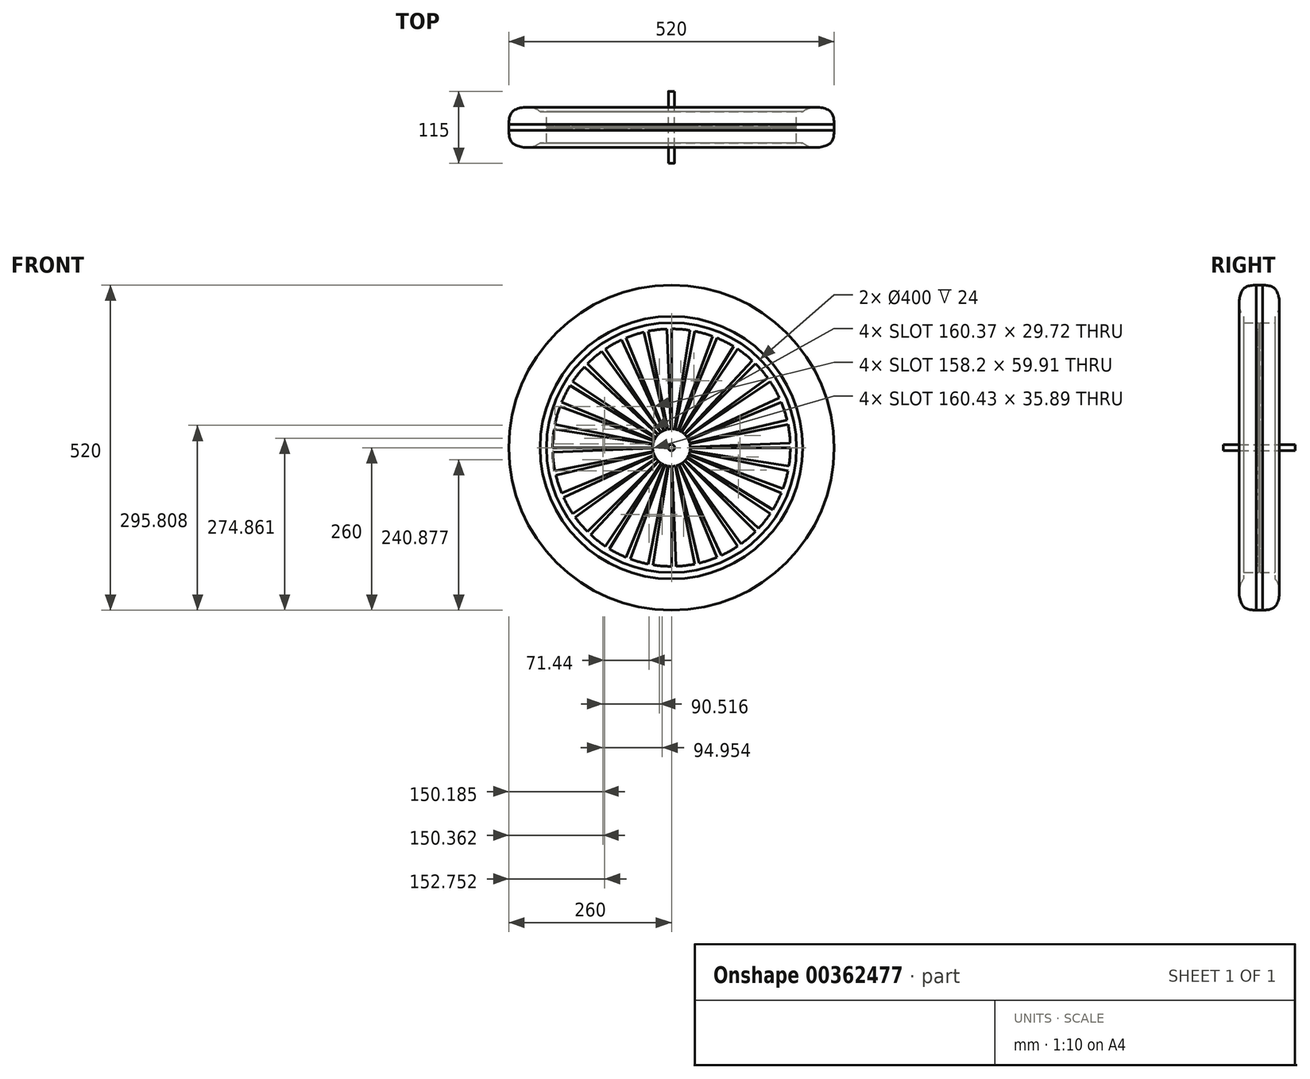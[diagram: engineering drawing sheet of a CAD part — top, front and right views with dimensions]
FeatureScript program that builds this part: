
annotation { "Feature Type Name" : "Feature", "Feature Type Description" : "" }
export const myFeature = defineFeature(function(context is Context, id is Id, definition is map)
    precondition{}
    {
        {
            var Q0;
            Q0=qCreatedBy(makeId("Right.planeOp"),FACE);
            var sketch = newSketch(context, id + "F0", { "sketchPlane" : qUnion([Q0])});
            skLineSegment(sketch, "E0", {"start": v(0, 0) * mm, "end": v(0, 200) * mm, "construction": true});
            skPoint(sketch, "E1.middle", {"position": v(0, 200) * mm});
            skPoint(sketch, "E2.visualSharp", {"position": v(-30.2, 260) * mm});
            skLineSegment(sketch, "E3.left", {"start": v(-1, 200) * mm, "end": v(-1, 5) * mm});
            skLineSegment(sketch, "E4.trimOffspring", {"start": v(-1, 200) * mm, "end": v(-25, 200) * mm});
            skLineSegment(sketch, "E5", {"start": v(-25, 200) * mm, "end": v(-25, 210) * mm});
            skFitSpline(sketch, "E6", {"points": [v(-5, 260) * mm, v(-25.83, 253.38) * mm, v(-32.03, 227.8) * mm, v(-25, 210) * mm], "startDerivative": vector(-86.17, -1.88) * mm, "endDerivative": vector(37.49, -43.12) * mm});
            skLineSegment(sketch, "E7", {"start": v(0, 260) * mm, "end": v(-5, 260) * mm});
            skLineSegment(sketch, "E8", {"start": v(0, 0) * mm, "end": v(-57.5, 0) * mm});
            skLineSegment(sketch, "E9", {"start": v(-57.5, 0) * mm, "end": v(-57.5, 5) * mm});
            skLineSegment(sketch, "E10.MirrorCS", {"start": v(0, 260) * mm, "end": v(5, 260) * mm});
            skLineSegment(sketch, "E11.MirrorCS", {"start": v(25, 200) * mm, "end": v(25, 210) * mm});
            skLineSegment(sketch, "E12.MirrorCS", {"start": v(1, 200) * mm, "end": v(25, 200) * mm});
            skFitSpline(sketch, "E13.MirrorCS", {"points": [v(5, 260) * mm, v(25.83, 253.38) * mm, v(32.03, 227.8) * mm, v(25, 210) * mm], "startDerivative": vector(86.17, -1.88) * mm, "endDerivative": vector(-37.49, -43.12) * mm});
            skLineSegment(sketch, "E14.MirrorCS", {"start": v(57.5, 0) * mm, "end": v(57.5, 5) * mm});
            skLineSegment(sketch, "E15.MirrorCS", {"start": v(0, 0) * mm, "end": v(57.5, 0) * mm});
            skPoint(sketch, "E16.MirrorP", {"position": v(30.2, 260) * mm});
            skLineSegment(sketch, "E17", {"start": v(-57.5, 5) * mm, "end": v(-1, 5) * mm});
            skLineSegment(sketch, "E18.MirrorCS", {"start": v(57.5, 5) * mm, "end": v(1, 5) * mm});
            skLineSegment(sketch, "E19.MirrorCS", {"start": v(1, 200) * mm, "end": v(1, 5) * mm});
            skSolve(sketch);
        }
        {
            var Q0;
            Q0=makeQuery(id+"F0.imprint","IMPRINT",FACE,{"disambiguationData":[TD([[makeQuery(id+"F0.imprint","IMPRINT",EDGE,{"derivedFrom":sQuery(id+"F0.wireOp",EDGE,"E3.left")}),1.0]])]});
            var Q1;
            Q1=sQuery(id+"F0.wireOp",EDGE,"E8");
            revolve(context, id + "F1", {"entities" : qUnion([Q0]), "axis" : qUnion([Q1]), "revolveType" : RevolveType.FULL});
        }
        {
            var Q0;
            Q0=makeQuery(id+"F1.opRevolve","SWEPT_FACE",FACE,{"disambiguationData":[OSD([sQuery(id+"F0.wireOp",EDGE,"E3.left")])]});
            var sketch = newSketch(context, id + "F2", { "sketchPlane" : qUnion([Q0])});
            skLineSegment(sketch, "E20", {"start": v(0, 30) * mm, "end": v(0, 190) * mm});
            skArc(sketch, "E21", {"start": v(0, 30) * mm, "mid": v(2.35, 29.9) * mm, "end": v(4.7, 29.63) * mm});
            skArc(sketch, "E22", {"start": v(0, 190) * mm, "mid": v(14.9, 189.41) * mm, "end": v(29.72, 187.66) * mm});
            skLineSegment(sketch, "E23", {"start": v(4.7, 29.63) * mm, "end": v(29.72, 187.66) * mm});
            skLineSegment(sketch, "E24.1.0", {"start": v(-5.85, 29.42) * mm, "end": v(-37.07, 186.35) * mm});
            skArc(sketch, "E24.1.1", {"start": v(-37.07, 186.35) * mm, "mid": v(-22.33, 188.68) * mm, "end": v(-7.46, 189.85) * mm});
            skLineSegment(sketch, "E24.1.2", {"start": v(-1.18, 29.98) * mm, "end": v(-7.46, 189.85) * mm});
            skArc(sketch, "E24.1.3", {"start": v(-5.85, 29.42) * mm, "mid": v(-3.53, 29.8) * mm, "end": v(-1.18, 29.98) * mm});
            skLineSegment(sketch, "E24.2.0", {"start": v(-11.48, 27.72) * mm, "end": v(-72.7, 175.54) * mm});
            skArc(sketch, "E24.2.1", {"start": v(-72.7, 175.54) * mm, "mid": v(-58.71, 180.7) * mm, "end": v(-44.35, 184.75) * mm});
            skLineSegment(sketch, "E24.2.2", {"start": v(-7, 29.17) * mm, "end": v(-44.35, 184.75) * mm});
            skArc(sketch, "E24.2.3", {"start": v(-11.48, 27.72) * mm, "mid": v(-9.27, 28.53) * mm, "end": v(-7, 29.17) * mm});
            skLineSegment(sketch, "E25.1.3.0", {"start": v(-16.67, 24.94) * mm, "end": v(-105.56, 157.98) * mm});
            skArc(sketch, "E25.3.3.0", {"start": v(-105.56, 157.98) * mm, "mid": v(-92.84, 165.77) * mm, "end": v(-79.55, 172.55) * mm});
            skLineSegment(sketch, "E25.7.3.0", {"start": v(-12.56, 27.24) * mm, "end": v(-79.55, 172.55) * mm});
            skArc(sketch, "E25.10.3.0", {"start": v(-16.67, 24.94) * mm, "mid": v(-14.66, 26.17) * mm, "end": v(-12.56, 27.24) * mm});
            skLineSegment(sketch, "E25.1.4.0", {"start": v(-21.21, 21.21) * mm, "end": v(-134.35, 134.35) * mm});
            skArc(sketch, "E25.3.4.0", {"start": v(-134.35, 134.35) * mm, "mid": v(-123.4, 144.48) * mm, "end": v(-111.68, 153.71) * mm});
            skLineSegment(sketch, "E25.7.4.0", {"start": v(-17.63, 24.27) * mm, "end": v(-111.68, 153.71) * mm});
            skArc(sketch, "E25.10.4.0", {"start": v(-21.21, 21.21) * mm, "mid": v(-19.48, 22.81) * mm, "end": v(-17.63, 24.27) * mm});
            skLineSegment(sketch, "E25.1.5.0", {"start": v(-24.94, 16.67) * mm, "end": v(-157.98, 105.56) * mm});
            skArc(sketch, "E25.3.5.0", {"start": v(-157.98, 105.56) * mm, "mid": v(-149.21, 117.63) * mm, "end": v(-139.52, 128.97) * mm});
            skLineSegment(sketch, "E25.7.5.0", {"start": v(-22.03, 20.36) * mm, "end": v(-139.52, 128.97) * mm});
            skArc(sketch, "E25.10.5.0", {"start": v(-24.94, 16.67) * mm, "mid": v(-23.56, 18.57) * mm, "end": v(-22.03, 20.36) * mm});
            skLineSegment(sketch, "E25.1.6.0", {"start": v(-27.72, 11.48) * mm, "end": v(-175.54, 72.7) * mm});
            skArc(sketch, "E25.3.6.0", {"start": v(-175.54, 72.7) * mm, "mid": v(-169.3, 86.26) * mm, "end": v(-162, 99.27) * mm});
            skLineSegment(sketch, "E25.7.6.0", {"start": v(-25.58, 15.67) * mm, "end": v(-162, 99.27) * mm});
            skArc(sketch, "E25.10.6.0", {"start": v(-27.72, 11.48) * mm, "mid": v(-26.73, 13.62) * mm, "end": v(-25.58, 15.67) * mm});
            skLineSegment(sketch, "E25.1.7.0", {"start": v(-29.42, 5.85) * mm, "end": v(-186.35, 37.07) * mm});
            skArc(sketch, "E25.3.7.0", {"start": v(-186.35, 37.07) * mm, "mid": v(-182.87, 51.57) * mm, "end": v(-178.26, 65.76) * mm});
            skLineSegment(sketch, "E25.7.7.0", {"start": v(-28.15, 10.38) * mm, "end": v(-178.26, 65.76) * mm});
            skArc(sketch, "E25.10.7.0", {"start": v(-29.42, 5.85) * mm, "mid": v(-28.87, 8.14) * mm, "end": v(-28.15, 10.38) * mm});
            skLineSegment(sketch, "E25.1.8.0", {"start": v(-30, 0) * mm, "end": v(-190, 0) * mm});
            skArc(sketch, "E25.3.8.0", {"start": v(-190, 0) * mm, "mid": v(-189.41, 14.9) * mm, "end": v(-187.66, 29.72) * mm});
            skLineSegment(sketch, "E25.7.8.0", {"start": v(-29.63, 4.7) * mm, "end": v(-187.66, 29.72) * mm});
            skArc(sketch, "E25.10.8.0", {"start": v(-30, 0) * mm, "mid": v(-29.9, 2.35) * mm, "end": v(-29.63, 4.7) * mm});
            skLineSegment(sketch, "E25.1.9.0", {"start": v(-29.42, -5.85) * mm, "end": v(-186.35, -37.07) * mm});
            skArc(sketch, "E25.3.9.0", {"start": v(-186.35, -37.07) * mm, "mid": v(-188.68, -22.33) * mm, "end": v(-189.85, -7.46) * mm});
            skLineSegment(sketch, "E25.7.9.0", {"start": v(-29.98, -1.18) * mm, "end": v(-189.85, -7.46) * mm});
            skArc(sketch, "E25.10.9.0", {"start": v(-29.42, -5.85) * mm, "mid": v(-29.8, -3.53) * mm, "end": v(-29.98, -1.18) * mm});
            skLineSegment(sketch, "E25.1.10.0", {"start": v(-27.72, -11.48) * mm, "end": v(-175.54, -72.7) * mm});
            skArc(sketch, "E25.3.10.0", {"start": v(-175.54, -72.7) * mm, "mid": v(-180.7, -58.71) * mm, "end": v(-184.75, -44.35) * mm});
            skLineSegment(sketch, "E25.7.10.0", {"start": v(-29.17, -7) * mm, "end": v(-184.75, -44.35) * mm});
            skArc(sketch, "E25.10.10.0", {"start": v(-27.72, -11.48) * mm, "mid": v(-28.53, -9.27) * mm, "end": v(-29.17, -7) * mm});
            skLineSegment(sketch, "E25.1.11.0", {"start": v(-24.94, -16.67) * mm, "end": v(-157.98, -105.56) * mm});
            skArc(sketch, "E25.3.11.0", {"start": v(-157.98, -105.56) * mm, "mid": v(-165.77, -92.84) * mm, "end": v(-172.55, -79.55) * mm});
            skLineSegment(sketch, "E25.7.11.0", {"start": v(-27.24, -12.56) * mm, "end": v(-172.55, -79.55) * mm});
            skArc(sketch, "E25.10.11.0", {"start": v(-24.94, -16.67) * mm, "mid": v(-26.17, -14.66) * mm, "end": v(-27.24, -12.56) * mm});
            skLineSegment(sketch, "E25.1.12.0", {"start": v(-21.21, -21.21) * mm, "end": v(-134.35, -134.35) * mm});
            skArc(sketch, "E25.3.12.0", {"start": v(-134.35, -134.35) * mm, "mid": v(-144.48, -123.4) * mm, "end": v(-153.71, -111.68) * mm});
            skLineSegment(sketch, "E25.7.12.0", {"start": v(-24.27, -17.63) * mm, "end": v(-153.71, -111.68) * mm});
            skArc(sketch, "E25.10.12.0", {"start": v(-21.21, -21.21) * mm, "mid": v(-22.81, -19.48) * mm, "end": v(-24.27, -17.63) * mm});
            skLineSegment(sketch, "E25.1.13.0", {"start": v(-16.67, -24.94) * mm, "end": v(-105.56, -157.98) * mm});
            skArc(sketch, "E25.3.13.0", {"start": v(-105.56, -157.98) * mm, "mid": v(-117.63, -149.21) * mm, "end": v(-128.97, -139.52) * mm});
            skLineSegment(sketch, "E25.7.13.0", {"start": v(-20.36, -22.03) * mm, "end": v(-128.97, -139.52) * mm});
            skArc(sketch, "E25.10.13.0", {"start": v(-16.67, -24.94) * mm, "mid": v(-18.57, -23.56) * mm, "end": v(-20.36, -22.03) * mm});
            skLineSegment(sketch, "E25.1.14.0", {"start": v(-11.48, -27.72) * mm, "end": v(-72.7, -175.54) * mm});
            skArc(sketch, "E25.3.14.0", {"start": v(-72.7, -175.54) * mm, "mid": v(-86.26, -169.3) * mm, "end": v(-99.27, -162) * mm});
            skLineSegment(sketch, "E25.7.14.0", {"start": v(-15.67, -25.58) * mm, "end": v(-99.27, -162) * mm});
            skArc(sketch, "E25.10.14.0", {"start": v(-11.48, -27.72) * mm, "mid": v(-13.62, -26.73) * mm, "end": v(-15.67, -25.58) * mm});
            skLineSegment(sketch, "E25.1.15.0", {"start": v(-5.85, -29.42) * mm, "end": v(-37.07, -186.35) * mm});
            skArc(sketch, "E25.3.15.0", {"start": v(-37.07, -186.35) * mm, "mid": v(-51.57, -182.87) * mm, "end": v(-65.76, -178.26) * mm});
            skLineSegment(sketch, "E25.7.15.0", {"start": v(-10.38, -28.15) * mm, "end": v(-65.76, -178.26) * mm});
            skArc(sketch, "E25.10.15.0", {"start": v(-5.85, -29.42) * mm, "mid": v(-8.14, -28.87) * mm, "end": v(-10.38, -28.15) * mm});
            skLineSegment(sketch, "E25.1.16.0", {"start": v(0, -30) * mm, "end": v(0, -190) * mm});
            skArc(sketch, "E25.3.16.0", {"start": v(0, -190) * mm, "mid": v(-14.9, -189.41) * mm, "end": v(-29.72, -187.66) * mm});
            skLineSegment(sketch, "E25.7.16.0", {"start": v(-4.7, -29.63) * mm, "end": v(-29.72, -187.66) * mm});
            skArc(sketch, "E25.10.16.0", {"start": v(0, -30) * mm, "mid": v(-2.35, -29.9) * mm, "end": v(-4.7, -29.63) * mm});
            skLineSegment(sketch, "E25.1.17.0", {"start": v(5.85, -29.42) * mm, "end": v(37.07, -186.35) * mm});
            skArc(sketch, "E25.3.17.0", {"start": v(37.07, -186.35) * mm, "mid": v(22.33, -188.68) * mm, "end": v(7.46, -189.85) * mm});
            skLineSegment(sketch, "E25.7.17.0", {"start": v(1.18, -29.98) * mm, "end": v(7.46, -189.85) * mm});
            skArc(sketch, "E25.10.17.0", {"start": v(5.85, -29.42) * mm, "mid": v(3.53, -29.8) * mm, "end": v(1.18, -29.98) * mm});
            skLineSegment(sketch, "E26.1.18.0", {"start": v(11.48, -27.72) * mm, "end": v(72.7, -175.54) * mm});
            skArc(sketch, "E26.3.18.0", {"start": v(72.7, -175.54) * mm, "mid": v(58.71, -180.7) * mm, "end": v(44.35, -184.75) * mm});
            skLineSegment(sketch, "E26.7.18.0", {"start": v(7, -29.17) * mm, "end": v(44.35, -184.75) * mm});
            skArc(sketch, "E26.10.18.0", {"start": v(11.48, -27.72) * mm, "mid": v(9.27, -28.53) * mm, "end": v(7, -29.17) * mm});
            skLineSegment(sketch, "E26.1.19.0", {"start": v(16.67, -24.94) * mm, "end": v(105.56, -157.98) * mm});
            skArc(sketch, "E26.3.19.0", {"start": v(105.56, -157.98) * mm, "mid": v(92.84, -165.77) * mm, "end": v(79.55, -172.55) * mm});
            skLineSegment(sketch, "E26.7.19.0", {"start": v(12.56, -27.24) * mm, "end": v(79.55, -172.55) * mm});
            skArc(sketch, "E26.10.19.0", {"start": v(16.67, -24.94) * mm, "mid": v(14.66, -26.17) * mm, "end": v(12.56, -27.24) * mm});
            skLineSegment(sketch, "E26.1.20.0", {"start": v(21.21, -21.21) * mm, "end": v(134.35, -134.35) * mm});
            skArc(sketch, "E26.3.20.0", {"start": v(134.35, -134.35) * mm, "mid": v(123.4, -144.48) * mm, "end": v(111.68, -153.71) * mm});
            skLineSegment(sketch, "E26.7.20.0", {"start": v(17.63, -24.27) * mm, "end": v(111.68, -153.71) * mm});
            skArc(sketch, "E26.10.20.0", {"start": v(21.21, -21.21) * mm, "mid": v(19.48, -22.81) * mm, "end": v(17.63, -24.27) * mm});
            skLineSegment(sketch, "E26.1.21.0", {"start": v(24.94, -16.67) * mm, "end": v(157.98, -105.56) * mm});
            skArc(sketch, "E26.3.21.0", {"start": v(157.98, -105.56) * mm, "mid": v(149.21, -117.63) * mm, "end": v(139.52, -128.97) * mm});
            skLineSegment(sketch, "E26.7.21.0", {"start": v(22.03, -20.36) * mm, "end": v(139.52, -128.97) * mm});
            skArc(sketch, "E26.10.21.0", {"start": v(24.94, -16.67) * mm, "mid": v(23.56, -18.57) * mm, "end": v(22.03, -20.36) * mm});
            skLineSegment(sketch, "E26.1.22.0", {"start": v(27.72, -11.48) * mm, "end": v(175.54, -72.7) * mm});
            skArc(sketch, "E26.3.22.0", {"start": v(175.54, -72.7) * mm, "mid": v(169.3, -86.26) * mm, "end": v(162, -99.27) * mm});
            skLineSegment(sketch, "E26.7.22.0", {"start": v(25.58, -15.67) * mm, "end": v(162, -99.27) * mm});
            skArc(sketch, "E26.10.22.0", {"start": v(27.72, -11.48) * mm, "mid": v(26.73, -13.62) * mm, "end": v(25.58, -15.67) * mm});
            skLineSegment(sketch, "E26.1.23.0", {"start": v(29.42, -5.85) * mm, "end": v(186.35, -37.07) * mm});
            skArc(sketch, "E26.3.23.0", {"start": v(186.35, -37.07) * mm, "mid": v(182.87, -51.57) * mm, "end": v(178.26, -65.76) * mm});
            skLineSegment(sketch, "E26.7.23.0", {"start": v(28.15, -10.38) * mm, "end": v(178.26, -65.76) * mm});
            skArc(sketch, "E26.10.23.0", {"start": v(29.42, -5.85) * mm, "mid": v(28.87, -8.14) * mm, "end": v(28.15, -10.38) * mm});
            skLineSegment(sketch, "E26.1.24.0", {"start": v(30, 0) * mm, "end": v(190, 0) * mm});
            skArc(sketch, "E26.3.24.0", {"start": v(190, 0) * mm, "mid": v(189.41, -14.9) * mm, "end": v(187.66, -29.72) * mm});
            skLineSegment(sketch, "E26.7.24.0", {"start": v(29.63, -4.7) * mm, "end": v(187.66, -29.72) * mm});
            skArc(sketch, "E26.10.24.0", {"start": v(30, 0) * mm, "mid": v(29.9, -2.35) * mm, "end": v(29.63, -4.7) * mm});
            skLineSegment(sketch, "E26.1.25.0", {"start": v(29.42, 5.85) * mm, "end": v(186.35, 37.07) * mm});
            skArc(sketch, "E26.3.25.0", {"start": v(186.35, 37.07) * mm, "mid": v(188.68, 22.33) * mm, "end": v(189.85, 7.46) * mm});
            skLineSegment(sketch, "E26.7.25.0", {"start": v(29.98, 1.18) * mm, "end": v(189.85, 7.46) * mm});
            skArc(sketch, "E26.10.25.0", {"start": v(29.42, 5.85) * mm, "mid": v(29.8, 3.53) * mm, "end": v(29.98, 1.18) * mm});
            skLineSegment(sketch, "E26.1.26.0", {"start": v(27.72, 11.48) * mm, "end": v(175.54, 72.7) * mm});
            skArc(sketch, "E26.3.26.0", {"start": v(175.54, 72.7) * mm, "mid": v(180.7, 58.71) * mm, "end": v(184.75, 44.35) * mm});
            skLineSegment(sketch, "E26.7.26.0", {"start": v(29.17, 7) * mm, "end": v(184.75, 44.35) * mm});
            skArc(sketch, "E26.10.26.0", {"start": v(27.72, 11.48) * mm, "mid": v(28.53, 9.27) * mm, "end": v(29.17, 7) * mm});
            skLineSegment(sketch, "E26.1.27.0", {"start": v(24.94, 16.67) * mm, "end": v(157.98, 105.56) * mm});
            skArc(sketch, "E26.3.27.0", {"start": v(157.98, 105.56) * mm, "mid": v(165.77, 92.84) * mm, "end": v(172.55, 79.55) * mm});
            skLineSegment(sketch, "E26.7.27.0", {"start": v(27.24, 12.56) * mm, "end": v(172.55, 79.55) * mm});
            skArc(sketch, "E26.10.27.0", {"start": v(24.94, 16.67) * mm, "mid": v(26.17, 14.66) * mm, "end": v(27.24, 12.56) * mm});
            skLineSegment(sketch, "E26.1.28.0", {"start": v(21.21, 21.21) * mm, "end": v(134.35, 134.35) * mm});
            skArc(sketch, "E26.3.28.0", {"start": v(134.35, 134.35) * mm, "mid": v(144.48, 123.4) * mm, "end": v(153.71, 111.68) * mm});
            skLineSegment(sketch, "E26.7.28.0", {"start": v(24.27, 17.63) * mm, "end": v(153.71, 111.68) * mm});
            skArc(sketch, "E26.10.28.0", {"start": v(21.21, 21.21) * mm, "mid": v(22.81, 19.48) * mm, "end": v(24.27, 17.63) * mm});
            skLineSegment(sketch, "E26.1.29.0", {"start": v(16.67, 24.94) * mm, "end": v(105.56, 157.98) * mm});
            skArc(sketch, "E26.3.29.0", {"start": v(105.56, 157.98) * mm, "mid": v(117.63, 149.21) * mm, "end": v(128.97, 139.52) * mm});
            skLineSegment(sketch, "E26.7.29.0", {"start": v(20.36, 22.03) * mm, "end": v(128.97, 139.52) * mm});
            skArc(sketch, "E26.10.29.0", {"start": v(16.67, 24.94) * mm, "mid": v(18.57, 23.56) * mm, "end": v(20.36, 22.03) * mm});
            skLineSegment(sketch, "E26.1.30.0", {"start": v(11.48, 27.72) * mm, "end": v(72.7, 175.54) * mm});
            skArc(sketch, "E26.3.30.0", {"start": v(72.7, 175.54) * mm, "mid": v(86.26, 169.3) * mm, "end": v(99.27, 162) * mm});
            skLineSegment(sketch, "E26.7.30.0", {"start": v(15.67, 25.58) * mm, "end": v(99.27, 162) * mm});
            skArc(sketch, "E26.10.30.0", {"start": v(11.48, 27.72) * mm, "mid": v(13.62, 26.73) * mm, "end": v(15.67, 25.58) * mm});
            skLineSegment(sketch, "E26.1.31.0", {"start": v(5.85, 29.42) * mm, "end": v(37.07, 186.35) * mm});
            skArc(sketch, "E26.3.31.0", {"start": v(37.07, 186.35) * mm, "mid": v(51.57, 182.87) * mm, "end": v(65.76, 178.26) * mm});
            skLineSegment(sketch, "E26.7.31.0", {"start": v(10.38, 28.15) * mm, "end": v(65.76, 178.26) * mm});
            skArc(sketch, "E26.10.31.0", {"start": v(5.85, 29.42) * mm, "mid": v(8.14, 28.87) * mm, "end": v(10.38, 28.15) * mm});
            skSolve(sketch);
        }
        {
            var Q0;
            Q0=qSketchRegion(id+"F2",true);
            extrude(context, id + "F3", {"entities" : qUnion([Q0]), "operationType" : NewBodyOperationType.REMOVE, "oppositeDirection" : true, "depth" : 10 * mm});
        }
    });
